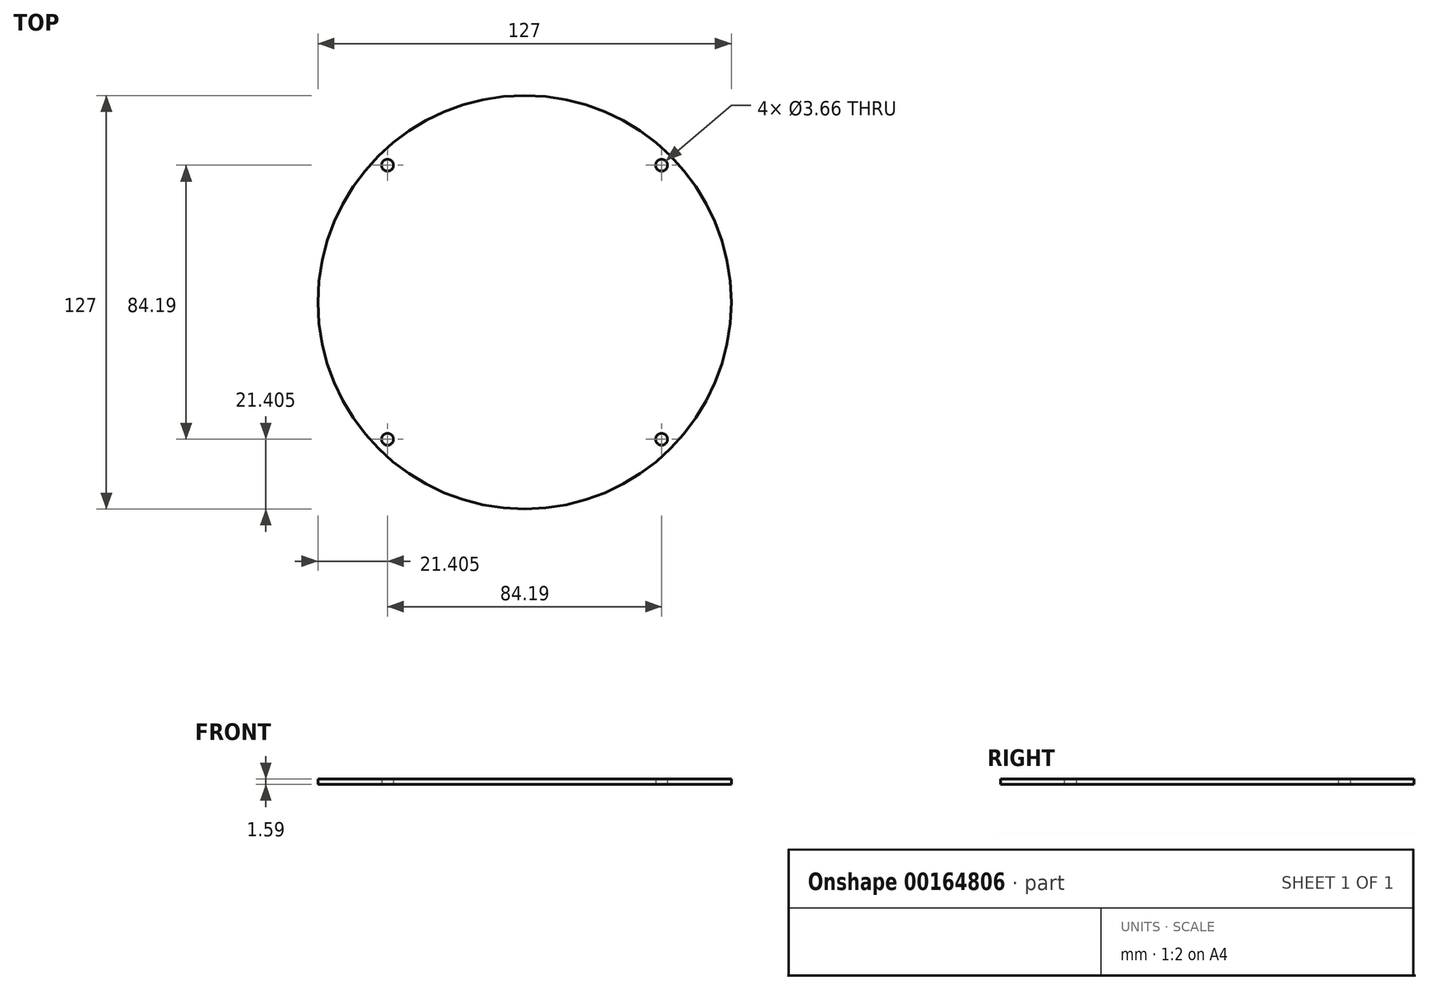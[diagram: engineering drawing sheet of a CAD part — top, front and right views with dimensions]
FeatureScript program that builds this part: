
annotation { "Feature Type Name" : "Feature", "Feature Type Description" : "" }
export const myFeature = defineFeature(function(context is Context, id is Id, definition is map)
    precondition{}
    {
        {
            var Q0;
            Q0=qCreatedBy(makeId("Top.planeOp"),FACE);
            var sketch = newSketch(context, id + "F0", { "sketchPlane" : qUnion([Q0])});
            skCircle(sketch, "E0", {"center": v(0, 0) * mm, "radius": 63.5 * mm});
            skLineSegment(sketch, "E1.bottom", {"start": v(42.1, 42.1) * mm, "end": v(-42.1, 42.1) * mm, "construction": true});
            skLineSegment(sketch, "E1.top", {"start": v(42.1, -42.1) * mm, "end": v(-42.1, -42.1) * mm, "construction": true});
            skLineSegment(sketch, "E1.left", {"start": v(42.1, 42.1) * mm, "end": v(42.1, -42.1) * mm, "construction": true});
            skLineSegment(sketch, "E1.right", {"start": v(-42.1, 42.1) * mm, "end": v(-42.1, -42.1) * mm, "construction": true});
            skCircle(sketch, "E2", {"center": v(42.1, 42.1) * mm, "radius": 3.97 * mm, "construction": true});
            skCircle(sketch, "E3", {"center": v(-42.1, 42.1) * mm, "radius": 1.83 * mm});
            skCircle(sketch, "E4", {"center": v(42.1, 42.1) * mm, "radius": 1.83 * mm});
            skCircle(sketch, "E5", {"center": v(42.1, -42.1) * mm, "radius": 1.83 * mm});
            skCircle(sketch, "E6", {"center": v(-42.1, -42.1) * mm, "radius": 1.83 * mm});
            skSolve(sketch);
        }
        {
            var Q0;
            Q0=qSketchRegion(id+"F0",true);
            extrude(context, id + "F1", {"entities" : qUnion([Q0]), "depth" : 1.59 * mm});
        }
    });
